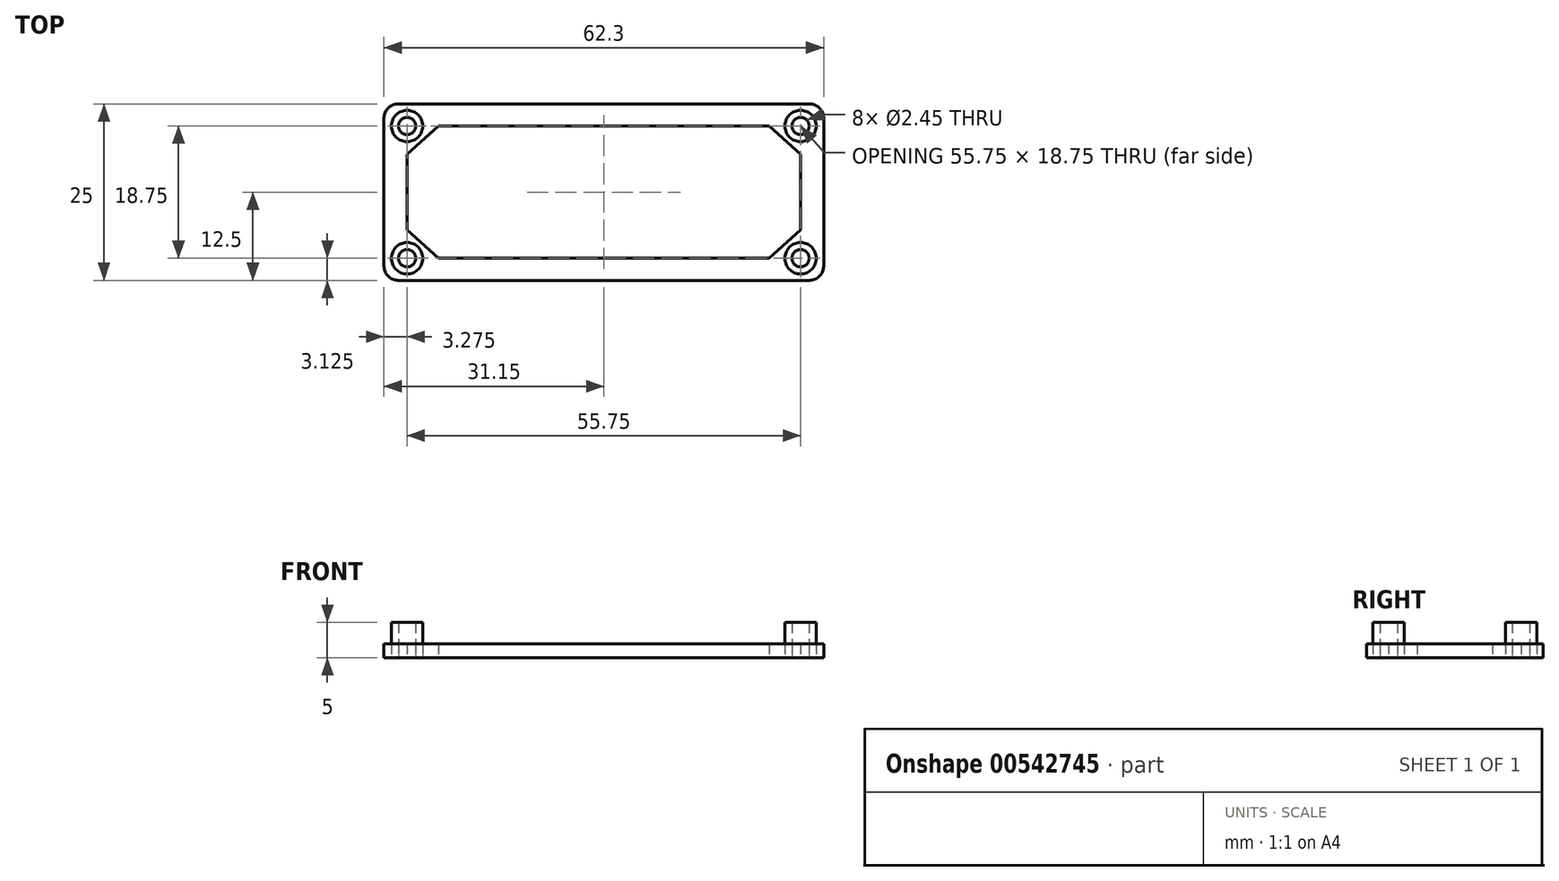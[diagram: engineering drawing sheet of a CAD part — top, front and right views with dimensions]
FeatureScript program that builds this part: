
annotation { "Feature Type Name" : "Feature", "Feature Type Description" : "" }
export const myFeature = defineFeature(function(context is Context, id is Id, definition is map)
    precondition{}
    {
        {
            var Q0;
            Q0=qCreatedBy(makeId("Top.planeOp"),FACE);
            var sketch = newSketch(context, id + "F0", { "sketchPlane" : qUnion([Q0])});
            skLineSegment(sketch, "E0.bottom", {"start": v(-31.15, 12.5) * mm, "end": v(31.15, 12.5) * mm});
            skLineSegment(sketch, "E0.top", {"start": v(-31.15, -12.5) * mm, "end": v(31.15, -12.5) * mm});
            skLineSegment(sketch, "E0.left", {"start": v(-31.15, 12.5) * mm, "end": v(-31.15, -12.5) * mm});
            skLineSegment(sketch, "E0.right", {"start": v(31.15, 12.5) * mm, "end": v(31.15, -12.5) * mm});
            skPoint(sketch, "E0.middle", {"position": v(0, 0) * mm});
            skCircle(sketch, "E1", {"center": v(-27.87, 9.38) * mm, "radius": 1.23 * mm});
            skCircle(sketch, "E2", {"center": v(-27.87, -9.38) * mm, "radius": 1.23 * mm});
            skCircle(sketch, "E3", {"center": v(27.87, 9.38) * mm, "radius": 1.23 * mm});
            skCircle(sketch, "E4", {"center": v(27.87, -9.38) * mm, "radius": 1.23 * mm});
            skLineSegment(sketch, "E5", {"start": v(-23.43, 9.38) * mm, "end": v(23.43, 9.38) * mm});
            skLineSegment(sketch, "E6", {"start": v(23.43, 9.38) * mm, "end": v(27.88, 5.35) * mm});
            skLineSegment(sketch, "E7", {"start": v(27.87, 5.35) * mm, "end": v(27.87, -5.35) * mm});
            skLineSegment(sketch, "E8", {"start": v(27.88, -5.35) * mm, "end": v(23.43, -9.38) * mm});
            skLineSegment(sketch, "E9", {"start": v(23.43, -9.38) * mm, "end": v(-23.43, -9.38) * mm});
            skLineSegment(sketch, "E10", {"start": v(-23.43, -9.38) * mm, "end": v(-27.88, -5.35) * mm});
            skLineSegment(sketch, "E11", {"start": v(-27.87, -5.35) * mm, "end": v(-27.87, 5.35) * mm});
            skLineSegment(sketch, "E12", {"start": v(-27.88, 5.35) * mm, "end": v(-23.43, 9.38) * mm});
            skCircle(sketch, "E13", {"center": v(-27.87, 9.38) * mm, "radius": 2.23 * mm});
            skCircle(sketch, "E14", {"center": v(-27.87, -9.38) * mm, "radius": 2.23 * mm});
            skCircle(sketch, "E15", {"center": v(27.87, 9.38) * mm, "radius": 2.23 * mm});
            skCircle(sketch, "E16", {"center": v(27.87, -9.38) * mm, "radius": 2.23 * mm});
            skSolve(sketch);
        }
        {
            var Q0;
            Q0=makeQuery(id+"F0.imprint","IMPRINT",FACE,{"disambiguationData":[TD([[makeQuery(id+"F0.imprint","IMPRINT",EDGE,{"derivedFrom":sQuery(id+"F0.wireOp",EDGE,"E1")}),-1.0]])]});
            var Q1;
            Q1=makeQuery(id+"F0.imprint","IMPRINT",FACE,{"disambiguationData":[TD([[makeQuery(id+"F0.imprint","IMPRINT",EDGE,{"derivedFrom":sQuery(id+"F0.wireOp",EDGE,"E0.bottom")}),-1.0]])]});
            var Q2;
            Q2=makeQuery(id+"F0.imprint","IMPRINT",FACE,{"disambiguationData":[TD([[makeQuery(id+"F0.imprint","IMPRINT",EDGE,{"derivedFrom":sQuery(id+"F0.wireOp",EDGE,"E2")}),-1.0]])]});
            var Q3;
            Q3=makeQuery(id+"F0.imprint","IMPRINT",FACE,{"disambiguationData":[TD([[makeQuery(id+"F0.imprint","IMPRINT",EDGE,{"derivedFrom":sQuery(id+"F0.wireOp",EDGE,"E3")}),-1.0]])]});
            var Q4;
            Q4=makeQuery(id+"F0.imprint","IMPRINT",FACE,{"disambiguationData":[TD([[makeQuery(id+"F0.imprint","IMPRINT",EDGE,{"derivedFrom":sQuery(id+"F0.wireOp",EDGE,"E4")}),-1.0]])]});
            extrude(context, id + "F1", {"entities" : qUnion([Q0, Q1, Q2, Q3, Q4]), "depth" : 2 * mm, "offsetDistance" : 25 * mm});
        }
        {
            var Q0;
            Q0=makeQuery(id+"F0.imprint","IMPRINT",FACE,{"disambiguationData":[TD([[makeQuery(id+"F0.imprint","IMPRINT",EDGE,{"derivedFrom":sQuery(id+"F0.wireOp",EDGE,"E1")}),-1.0]])]});
            var Q1;
            Q1=makeQuery(id+"F0.imprint","IMPRINT",FACE,{"disambiguationData":[TD([[makeQuery(id+"F0.imprint","IMPRINT",EDGE,{"derivedFrom":sQuery(id+"F0.wireOp",EDGE,"E2")}),-1.0]])]});
            var Q2;
            Q2=makeQuery(id+"F0.imprint","IMPRINT",FACE,{"disambiguationData":[TD([[makeQuery(id+"F0.imprint","IMPRINT",EDGE,{"derivedFrom":sQuery(id+"F0.wireOp",EDGE,"E3")}),-1.0]])]});
            var Q3;
            Q3=makeQuery(id+"F0.imprint","IMPRINT",FACE,{"disambiguationData":[TD([[makeQuery(id+"F0.imprint","IMPRINT",EDGE,{"derivedFrom":sQuery(id+"F0.wireOp",EDGE,"E4")}),-1.0]])]});
            extrude(context, id + "F2", {"entities" : qUnion([Q0, Q1, Q2, Q3]), "depth" : 5 * mm, "offsetDistance" : 25 * mm});
        }
        {
            var Q0;
            Q0=makeQuery(id+"F1.opExtrude","SWEPT_EDGE",EDGE,{"disambiguationData":[OSD([sQuery(id+"F0.wireOp",EDGE,"E0.top"),sQuery(id+"F0.wireOp",EDGE,"E0.left")])]});
            var Q1;
            Q1=makeQuery(id+"F1.opExtrude","SWEPT_EDGE",EDGE,{"disambiguationData":[OSD([sQuery(id+"F0.wireOp",EDGE,"E0.bottom"),sQuery(id+"F0.wireOp",EDGE,"E0.left")])]});
            var Q2;
            Q2=makeQuery(id+"F1.opExtrude","SWEPT_EDGE",EDGE,{"disambiguationData":[OSD([sQuery(id+"F0.wireOp",EDGE,"E0.bottom"),sQuery(id+"F0.wireOp",EDGE,"E0.right")])]});
            var Q3;
            Q3=makeQuery(id+"F1.opExtrude","SWEPT_EDGE",EDGE,{"disambiguationData":[OSD([sQuery(id+"F0.wireOp",EDGE,"E0.top"),sQuery(id+"F0.wireOp",EDGE,"E0.right")])]});
            fillet(context, id + "F3", {"entities" : qUnion([Q0, Q1, Q2, Q3]), "radius" : 2 * mm, "tangentPropagation" : true, "allowEdgeOverflow" : false});
        }
    });
